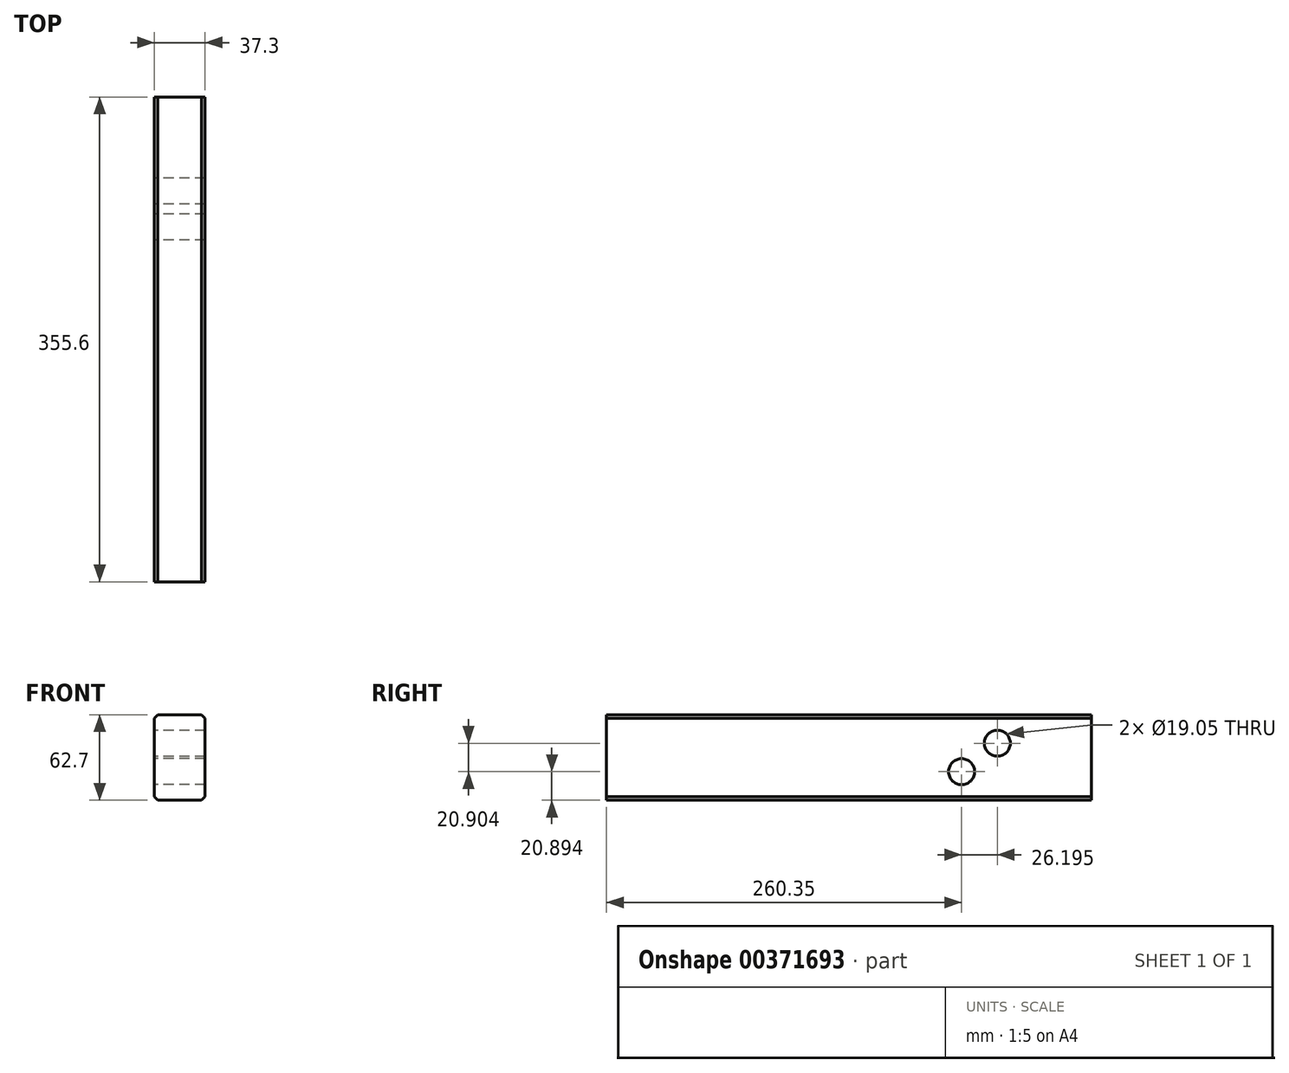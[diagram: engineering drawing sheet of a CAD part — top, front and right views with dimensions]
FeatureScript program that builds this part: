
annotation { "Feature Type Name" : "Feature", "Feature Type Description" : "" }
export const myFeature = defineFeature(function(context is Context, id is Id, definition is map)
    precondition{}
    {
        {
            var Q0;
            Q0=qCreatedBy(makeId("Front.planeOp"),FACE);
            var sketch = newSketch(context, id + "F0", { "sketchPlane" : qUnion([Q0])});
            skLineSegment(sketch, "E0.bottom", {"start": v(-1193.8, 31.35) * mm, "end": v(-1156.5, 31.35) * mm});
            skLineSegment(sketch, "E0.top", {"start": v(-1193.8, -31.35) * mm, "end": v(-1156.5, -31.35) * mm});
            skLineSegment(sketch, "E0.left", {"start": v(-1193.8, 31.35) * mm, "end": v(-1193.8, -31.35) * mm});
            skLineSegment(sketch, "E0.right", {"start": v(-1156.5, 31.35) * mm, "end": v(-1156.5, -31.35) * mm});
            skSolve(sketch);
        }
        {
            var Q0;
            Q0=makeQuery(id+"F0.imprint","IMPRINT",FACE,{"disambiguationData":[TD([[makeQuery(id+"F0.imprint","IMPRINT",EDGE,{"derivedFrom":sQuery(id+"F0.wireOp",EDGE,"E0.bottom")}),-1.0]])]});
            extrude(context, id + "F1", {"entities" : qUnion([Q0]), "depth" : 355.6 * mm});
        }
        {
            var Q0;
            Q0=makeQuery(id+"F1.opExtrude","SWEPT_FACE",FACE,{"disambiguationData":[OSD([sQuery(id+"F0.wireOp",EDGE,"E0.left")])]});
            var sketch = newSketch(context, id + "F2", { "sketchPlane" : qUnion([Q0])});
            skPoint(sketch, "E1", {"position": v(69.05, 10.45) * mm});
            skPoint(sketch, "E2", {"position": v(95.25, -10.46) * mm});
            skSolve(sketch);
        }
        {
            var Q0;
            Q0=sQuery(id+"F2.wireOp",VERTEX,"E1");
            var Q1;
            Q1=sQuery(id+"F2.wireOp",VERTEX,"E2");
            var Q2;
            Q2=makeQuery(id+"F1.opExtrude","SWEPT_BODY",BODY,{"disambiguationData":[OSD([sQuery(id+"F0.wireOp",EDGE,"E0.bottom"),sQuery(id+"F0.wireOp",EDGE,"E0.top"),sQuery(id+"F0.wireOp",EDGE,"E0.left"),sQuery(id+"F0.wireOp",EDGE,"E0.right")])]});
            hole(context, id + "F3", {"style" : HoleStyle.SIMPLE, "endStyle" : HoleEndStyle.THROUGH, "holeDiameter" : 19.05 * mm, "isTappedThrough" : true, "tappedDepth" : 12.7 * mm, "tapClearance" : 3, "locations" : qUnion([Q0, Q1]), "scope" : qUnion([Q2])});
        }
        {
            var Q0;
            Q0=makeQuery(id+"F1.opExtrude","SWEPT_EDGE",EDGE,{"disambiguationData":[OSD([sQuery(id+"F0.wireOp",EDGE,"E0.bottom"),sQuery(id+"F0.wireOp",EDGE,"E0.left")])]});
            var Q1;
            Q1=makeQuery(id+"F1.opExtrude","SWEPT_EDGE",EDGE,{"disambiguationData":[OSD([sQuery(id+"F0.wireOp",EDGE,"E0.bottom"),sQuery(id+"F0.wireOp",EDGE,"E0.right")])]});
            var Q2;
            Q2=makeQuery(id+"F1.opExtrude","SWEPT_EDGE",EDGE,{"disambiguationData":[OSD([sQuery(id+"F0.wireOp",EDGE,"E0.top"),sQuery(id+"F0.wireOp",EDGE,"E0.left")])]});
            var Q3;
            Q3=makeQuery(id+"F1.opExtrude","SWEPT_EDGE",EDGE,{"disambiguationData":[OSD([sQuery(id+"F0.wireOp",EDGE,"E0.top"),sQuery(id+"F0.wireOp",EDGE,"E0.right")])]});
            chamfer(context, id + "F4", {"entities" : qUnion([Q0, Q1, Q2, Q3]), "width" : 2.54 * mm, "tangentPropagation" : true});
        }
    });
